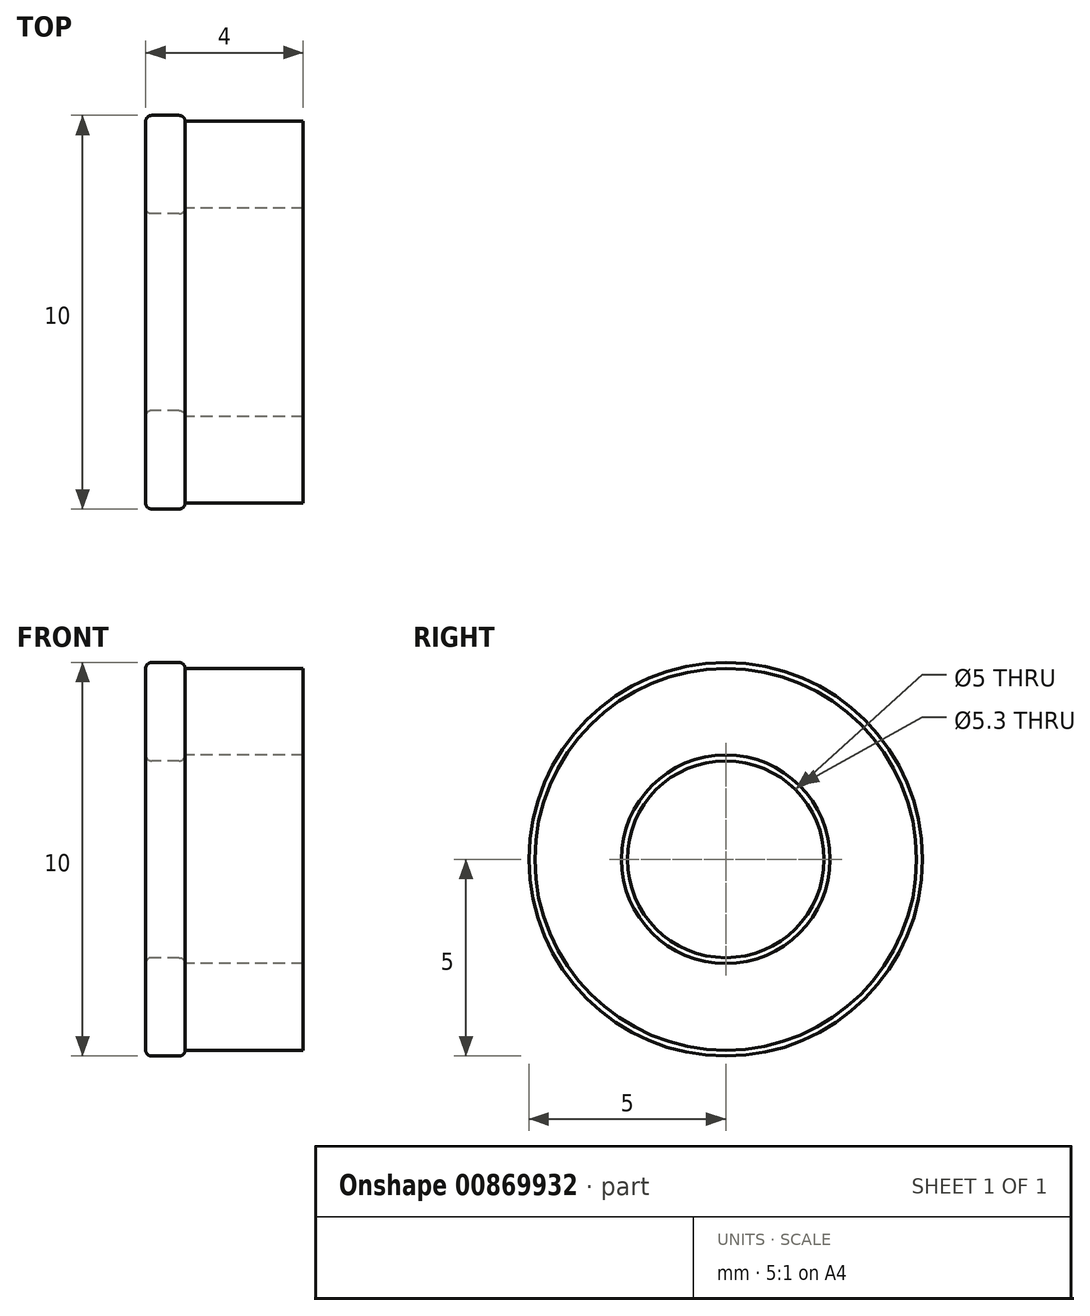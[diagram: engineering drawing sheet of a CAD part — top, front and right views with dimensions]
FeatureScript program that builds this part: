
annotation { "Feature Type Name" : "Feature", "Feature Type Description" : "" }
export const myFeature = defineFeature(function(context is Context, id is Id, definition is map)
    precondition{}
    {
        {
            var Q0;
            Q0=qCreatedBy(makeId("Top.planeOp"),FACE);
            var sketch = newSketch(context, id + "F0", { "sketchPlane" : qUnion([Q0])});
            skLineSegment(sketch, "E0.bottom", {"start": v(-0.35, 5) * mm, "end": v(0.35, 5) * mm});
            skLineSegment(sketch, "E0.top", {"start": v(-0.35, 2.5) * mm, "end": v(0.35, 2.5) * mm});
            skLineSegment(sketch, "E0.left", {"start": v(-0.5, 4.85) * mm, "end": v(-0.5, 2.65) * mm});
            skLineSegment(sketch, "E0.right", {"start": v(0.5, 4.85) * mm, "end": v(0.5, 2.65) * mm});
            skPoint(sketch, "E1", {"position": v(0, 2.5) * mm});
            skPoint(sketch, "E2.visualSharp", {"position": v(-0.5, 5) * mm});
            skArc(sketch, "E2.filletArc", {"start": v(-0.35, 5) * mm, "mid": v(-0.46, 4.96) * mm, "end": v(-0.5, 4.85) * mm});
            skPoint(sketch, "E3.visualSharp", {"position": v(0.5, 5) * mm});
            skArc(sketch, "E3.filletArc", {"start": v(0.5, 4.85) * mm, "mid": v(0.46, 4.96) * mm, "end": v(0.35, 5) * mm});
            skPoint(sketch, "E4.visualSharp", {"position": v(0.5, 2.5) * mm});
            skArc(sketch, "E4.filletArc", {"start": v(0.35, 2.5) * mm, "mid": v(0.46, 2.54) * mm, "end": v(0.5, 2.65) * mm});
            skPoint(sketch, "E5.visualSharp", {"position": v(-0.5, 2.5) * mm});
            skArc(sketch, "E5.filletArc", {"start": v(-0.5, 2.65) * mm, "mid": v(-0.46, 2.54) * mm, "end": v(-0.35, 2.5) * mm});
            skLineSegment(sketch, "E6", {"start": v(0, 0) * mm, "end": v(0.5, 0) * mm, "construction": true});
            skSolve(sketch);
        }
        {
            var Q0;
            Q0=makeQuery(id+"F0.imprint","IMPRINT",FACE,{"disambiguationData":[TD([[makeQuery(id+"F0.imprint","IMPRINT",EDGE,{"derivedFrom":sQuery(id+"F0.wireOp",EDGE,"E0.bottom")}),-1.0]])]});
            var Q1;
            Q1=sQuery(id+"F0.wireOp",EDGE,"E6");
            revolve(context, id + "F1", {"entities" : qUnion([Q0]), "axis" : qUnion([Q1]), "revolveType" : RevolveType.FULL});
        }
        {
            var Q0;
            Q0=makeQuery(id+"F1.opRevolve","SWEPT_FACE",FACE,{"disambiguationData":[OSD([sQuery(id+"F0.wireOp",EDGE,"E0.right")])]});
            extrude(context, id + "F2", {"entities" : qUnion([Q0]), "operationType" : NewBodyOperationType.ADD, "depth" : 3 * mm, "offsetDistance" : 25 * mm});
        }
    });
